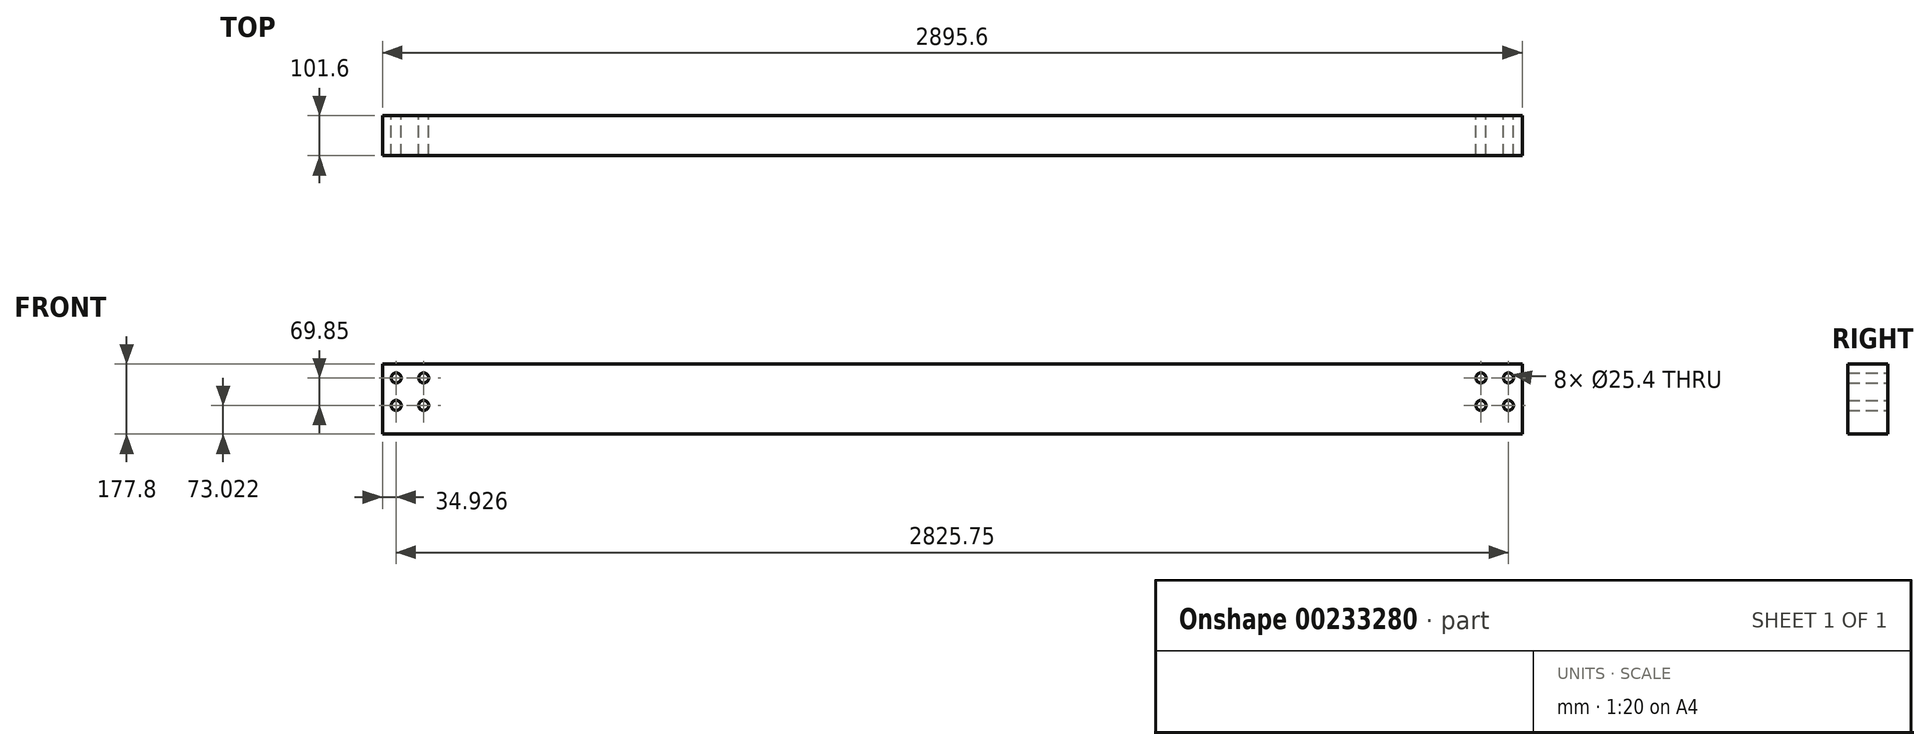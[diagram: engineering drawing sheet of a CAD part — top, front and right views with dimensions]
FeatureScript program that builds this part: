
annotation { "Feature Type Name" : "Feature", "Feature Type Description" : "" }
export const myFeature = defineFeature(function(context is Context, id is Id, definition is map)
    precondition{}
    {
        {
            var Q0;
            Q0=qCreatedBy(makeId("Front.planeOp"),FACE);
            var sketch = newSketch(context, id + "F0", { "sketchPlane" : qUnion([Q0])});
            skLineSegment(sketch, "E0.bottom", {"start": v(-1446.08, -363.77) * mm, "end": v(1449.52, -363.77) * mm});
            skLineSegment(sketch, "E0.top", {"start": v(-1446.08, -541.57) * mm, "end": v(1449.52, -541.57) * mm});
            skLineSegment(sketch, "E0.left", {"start": v(-1446.08, -363.77) * mm, "end": v(-1446.08, -541.57) * mm});
            skLineSegment(sketch, "E0.right", {"start": v(1449.52, -363.77) * mm, "end": v(1449.52, -541.57) * mm});
            skSolve(sketch);
        }
        {
            var Q0;
            Q0=makeQuery(id+"F0.imprint","IMPRINT",FACE,{"disambiguationData":[TD([[makeQuery(id+"F0.imprint","IMPRINT",EDGE,{"derivedFrom":sQuery(id+"F0.wireOp",EDGE,"E0.bottom")}),-1.0]])]});
            extrude(context, id + "F1", {"entities" : qUnion([Q0]), "depth" : 101.6 * mm});
        }
        {
            var Q0;
            Q0=makeQuery(id+"F1.opExtrude","CAP_FACE",FACE,{"disambiguationData":[OSD([sQuery(id+"F0.wireOp",EDGE,"E0.bottom"),sQuery(id+"F0.wireOp",EDGE,"E0.top"),sQuery(id+"F0.wireOp",EDGE,"E0.left"),sQuery(id+"F0.wireOp",EDGE,"E0.right")])],"isStart":true});
            var sketch = newSketch(context, id + "F2", { "sketchPlane" : qUnion([Q0])});
            skCircle(sketch, "E1", {"center": v(1341.3, -468.55) * mm, "radius": 12.7 * mm});
            skCircle(sketch, "E2", {"center": v(1341.3, -398.7) * mm, "radius": 12.7 * mm});
            skCircle(sketch, "E3", {"center": v(1411.15, -398.7) * mm, "radius": 12.7 * mm});
            skCircle(sketch, "E4", {"center": v(1411.15, -468.55) * mm, "radius": 12.7 * mm});
            skCircle(sketch, "E5", {"center": v(-1414.6, -468.55) * mm, "radius": 12.7 * mm});
            skCircle(sketch, "E6", {"center": v(-1414.6, -398.7) * mm, "radius": 12.7 * mm});
            skCircle(sketch, "E7", {"center": v(-1344.75, -468.55) * mm, "radius": 12.7 * mm});
            skCircle(sketch, "E8", {"center": v(-1344.75, -398.7) * mm, "radius": 12.7 * mm});
            skSolve(sketch);
        }
        {
            var Q0;
            Q0=sQuery(id+"F2.wireOp",VERTEX,"E5.center");
            var Q1;
            Q1=sQuery(id+"F2.wireOp",VERTEX,"E6.center");
            var Q2;
            Q2=sQuery(id+"F2.wireOp",VERTEX,"E8.center");
            var Q3;
            Q3=sQuery(id+"F2.wireOp",VERTEX,"E7.center");
            var Q4;
            Q4=sQuery(id+"F2.wireOp",VERTEX,"E2.center");
            var Q5;
            Q5=sQuery(id+"F2.wireOp",VERTEX,"E3.center");
            var Q6;
            Q6=sQuery(id+"F2.wireOp",VERTEX,"E4.center");
            var Q7;
            Q7=sQuery(id+"F2.wireOp",VERTEX,"E1.center");
            var Q8;
            Q8=makeQuery(id+"F1.opExtrude","SWEPT_BODY",BODY,{"disambiguationData":[OSD([sQuery(id+"F0.wireOp",EDGE,"E0.bottom"),sQuery(id+"F0.wireOp",EDGE,"E0.top"),sQuery(id+"F0.wireOp",EDGE,"E0.left"),sQuery(id+"F0.wireOp",EDGE,"E0.right")])]});
            hole(context, id + "F3", {"style" : HoleStyle.SIMPLE, "endStyle" : HoleEndStyle.THROUGH, "holeDiameter" : 25.4 * mm, "tappedDepth" : 12.7 * mm, "tapClearance" : 3, "locations" : qUnion([Q0, Q1, Q2, Q3, Q4, Q5, Q6, Q7]), "scope" : qUnion([Q8])});
        }
    });
